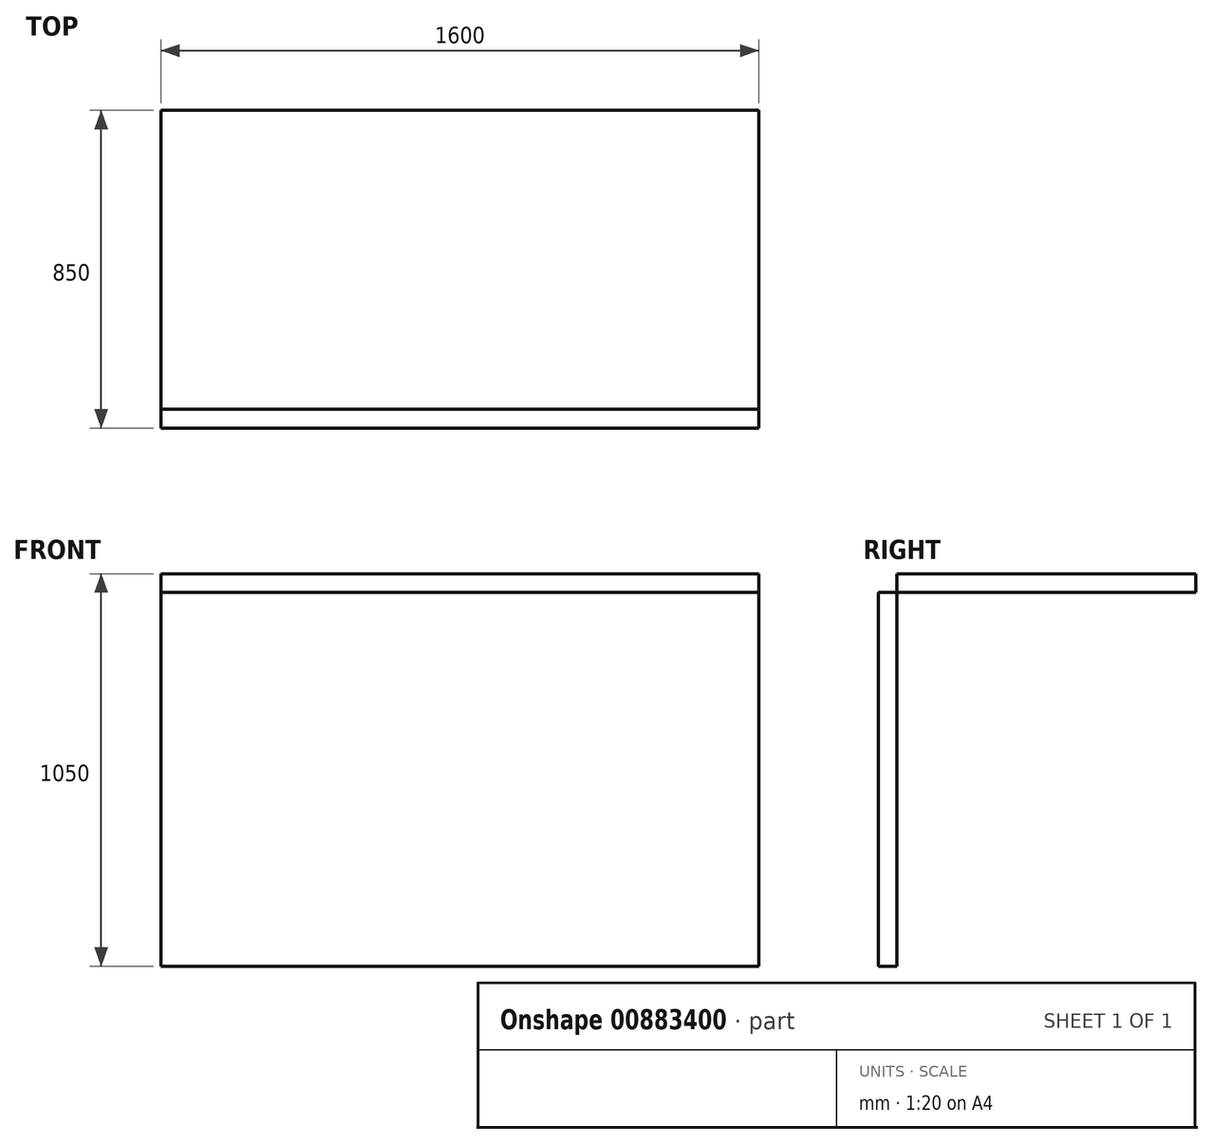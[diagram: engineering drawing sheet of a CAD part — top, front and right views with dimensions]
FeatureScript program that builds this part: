
annotation { "Feature Type Name" : "Feature", "Feature Type Description" : "" }
export const myFeature = defineFeature(function(context is Context, id is Id, definition is map)
    precondition{}
    {
        {
            var Q0;
            Q0=qCreatedBy(makeId("Front.planeOp"),FACE);
            var sketch = newSketch(context, id + "F0", { "sketchPlane" : qUnion([Q0])});
            skLineSegment(sketch, "E0", {"start": v(-19.1, 0) * mm, "end": v(1580.9, 0) * mm});
            skLineSegment(sketch, "E1", {"start": v(-19.1, 0) * mm, "end": v(-19.1, 1000) * mm});
            skLineSegment(sketch, "E2", {"start": v(1580.9, 0) * mm, "end": v(1580.9, 1000) * mm});
            skLineSegment(sketch, "E3", {"start": v(-19.1, 1000) * mm, "end": v(1580.9, 1000) * mm});
            skSolve(sketch);
        }
        {
            var Q0;
            Q0 = qSketchRegion(id + "F0", true);
            extrude(context, id + "F1", {"entities" : qUnion([Q0]), "depth" : 50 * mm, "offsetDistance" : 25 * mm});
        }
        {
            var Q0;
            Q0=makeQuery(id+"F1.opExtrude","SWEPT_FACE",FACE,{"disambiguationData":[OSD([sQuery(id+"F0.wireOp",EDGE,"E3")])]});
            var sketch = newSketch(context, id + "F2", { "sketchPlane" : qUnion([Q0])});
            skLineSegment(sketch, "E4", {"start": v(-19.1, 800) * mm, "end": v(1580.9, 800) * mm});
            skLineSegment(sketch, "E5", {"start": v(1580.9, 800) * mm, "end": v(1580.9, 0) * mm});
            skLineSegment(sketch, "E6", {"start": v(-19.1, 800) * mm, "end": v(-19.1, 0) * mm});
            skSolve(sketch);
        }
        {
            var Q0;
            Q0=makeQuery(id+"F2.imprint","IMPRINT",FACE,{"disambiguationData":[TD([[makeQuery(id+"F2.imprint","IMPRINT",EDGE,{"derivedFrom":sQuery(id+"F2.wireOp",EDGE,"E4")}),-1.0]])]});
            extrude(context, id + "F3", {"entities" : qUnion([Q0]), "depth" : 50 * mm, "offsetDistance" : 25 * mm});
        }
    });
